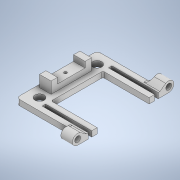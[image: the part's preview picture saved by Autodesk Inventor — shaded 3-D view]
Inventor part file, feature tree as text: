
AUTODESK INVENTOR PART (.ipt)
format: ipt  version: 2020 (Build 240168000, 168)  size: 278,016 bytes
history: native  units: in
note: dims shown in document units (in); Inventor stores cm internally (conversion verified against a paired STEP export)
features: extrude x5, sketch x3, fillet x1
ambient origin geometry x8: Origin, YZ Plane, XZ Plane, XY Plane, X Axis, Y Axis, Z Axis, Center Point
bodies: Solid1 (feature_tree)
feature tree (9):
  extrude  "Extrusion1"  Depth=2.7559in
  extrude  "Extrusion8"  Depth=0.315in
  extrude  "Extrusion9"  Depth=0.3937in
  extrude  "Extrusion5"  Depth=0.3937in
  extrude  "Extrusion6"  Depth=0.3937in
  fillet  "Fillet5"  Radius=0.0591in
  sketch  "Sketch5"  dims[d0=2.7559in d1=2.2638in]
  sketch  "Sketch6"  dims[d2=0.1875in d3=0.0in d4=0.315in]
  sketch  "Sketch9"  dims[d5=0.3937in d6=0.3937in d7=0.8858in d8=1.5748in d9=0.0591in d10=1.5748in d11=0.1181in d45=0.0in d46=0.1181in d47=0.9843in d48=0.0in d49=0.3543in d50=0.1969in d51=0.3937in d52=0.0in d53=0.1575in d65=0.0984in d67=1.378in d68=0.3937in d69=0.1969in d70=0.0in d73=0.1969in d74=0.0in d82=1.1811in d83=0.3937in d84=0.0984in d85=1.378in d86=0.3937in d87=0.2165in d88=0.2165in]
